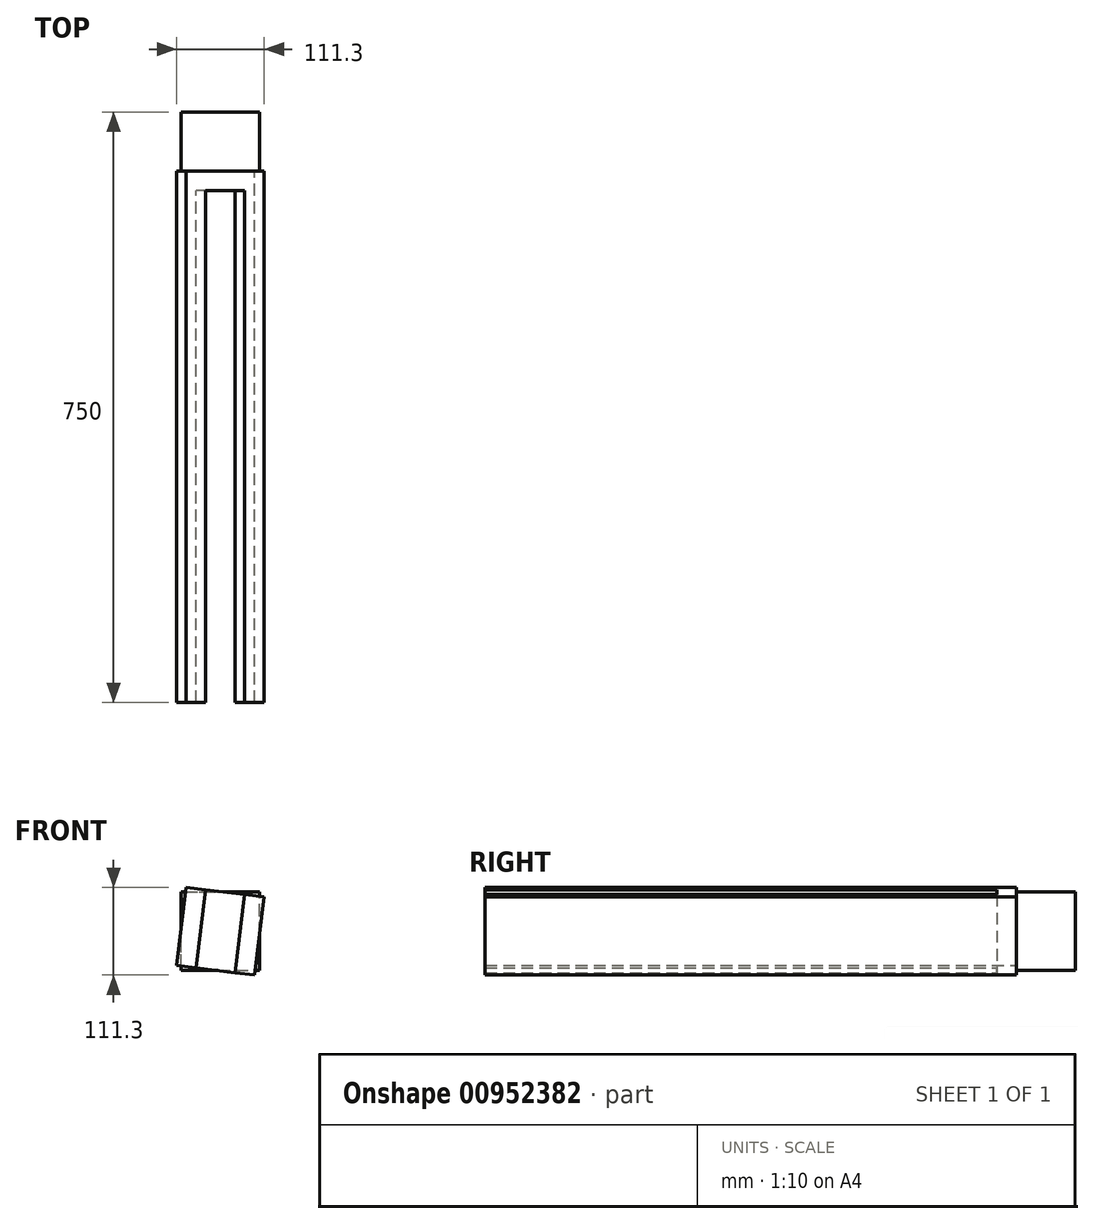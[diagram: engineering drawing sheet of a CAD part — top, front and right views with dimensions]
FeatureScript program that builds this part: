
annotation { "Feature Type Name" : "Feature", "Feature Type Description" : "" }
export const myFeature = defineFeature(function(context is Context, id is Id, definition is map)
    precondition{}
    {
        {
            var Q0;
            Q0=qCreatedBy(makeId("Front.planeOp"),FACE);
            var sketch = newSketch(context, id + "F0", { "sketchPlane" : qUnion([Q0])});
            skLineSegment(sketch, "E0.bottom", {"start": v(0, 0) * mm, "end": v(100, 0) * mm});
            skLineSegment(sketch, "E0.top", {"start": v(0, 100) * mm, "end": v(100, 100) * mm});
            skLineSegment(sketch, "E0.left", {"start": v(0, 0) * mm, "end": v(0, 100) * mm});
            skLineSegment(sketch, "E0.right", {"start": v(100, 0) * mm, "end": v(100, 100) * mm});
            skSolve(sketch);
        }
        {
            var Q0;
            Q0 = qSketchRegion(id + "F0", true);
            extrude(context, id + "F1", {"entities" : qUnion([Q0]), "depth" : 75 * mm, "offsetDistance" : 25 * mm});
        }
        {
            var Q0;
            Q0=makeQuery(id+"F1.opExtrude","CAP_FACE",FACE,{"disambiguationData":[OSD([sQuery(id+"F0.wireOp",EDGE,"E0.bottom"),sQuery(id+"F0.wireOp",EDGE,"E0.top"),sQuery(id+"F0.wireOp",EDGE,"E0.left"),sQuery(id+"F0.wireOp",EDGE,"E0.right")])],"isStart":false});
            var sketch = newSketch(context, id + "F2", { "sketchPlane" : qUnion([Q0])});
            skLineSegment(sketch, "E1", {"start": v(-5.65, 6.38) * mm, "end": v(6.38, 105.65) * mm});
            skLineSegment(sketch, "E2", {"start": v(6.38, 105.65) * mm, "end": v(105.65, 93.62) * mm});
            skLineSegment(sketch, "E3", {"start": v(105.65, 93.62) * mm, "end": v(93.62, -5.65) * mm});
            skLineSegment(sketch, "E4", {"start": v(93.62, -5.65) * mm, "end": v(-5.65, 6.38) * mm});
            skLineSegment(sketch, "E5", {"start": v(0, 100) * mm, "end": v(100, 0) * mm});
            skLineSegment(sketch, "E6", {"start": v(100, 0) * mm, "end": v(100, 100) * mm});
            skLineSegment(sketch, "E7", {"start": v(100, 100) * mm, "end": v(0, 0) * mm});
            skSolve(sketch);
        }
        {
            var Q0;
            {var subQ0=sQuery(id+"F2.wireOp",EDGE,"E3");var subQ1=sQuery(id+"F2.wireOp",EDGE,"E2");var subQ2=makeQuery(id+"F2.imprint","INTERSECT",VERTEX,{"derivedFrom":[subQ1,subQ0]});Q0=makeQuery(id+"F2.imprint","IMPRINT",FACE,{"disambiguationData":[TD([[makeQuery(id+"F2.imprint","IMPRINT",EDGE,{"disambiguationData":[TD([[subQ2,1.0]])],"derivedFrom":subQ1}),-1.0]])]});}
            var Q1;
            {var subQ5=sQuery(id+"F2.wireOp",EDGE,"E6");var subQ7=sQuery(id+"F2.wireOp",EDGE,"E2");var subQ8=makeQuery(id+"F2.imprint","INTERSECT",VERTEX,{"derivedFrom":[subQ7,subQ5]});Q1=makeQuery(id+"F2.imprint","IMPRINT",FACE,{"disambiguationData":[TD([[makeQuery(id+"F2.imprint","IMPRINT",EDGE,{"disambiguationData":[TD([[subQ8,1.0]])],"derivedFrom":subQ7}),-1.0]])]});}
            var Q2;
            {var subQ0=sQuery(id+"F2.wireOp",EDGE,"E4");var subQ1=sQuery(id+"F2.wireOp",EDGE,"E1");var subQ2=makeQuery(id+"F2.imprint","INTERSECT",VERTEX,{"derivedFrom":[subQ1,subQ0]});Q2=makeQuery(id+"F2.imprint","IMPRINT",FACE,{"disambiguationData":[TD([[makeQuery(id+"F2.imprint","IMPRINT",EDGE,{"disambiguationData":[TD([[subQ2,-1.0]])],"derivedFrom":subQ1}),-1.0]])]});}
            var Q3;
            {var subQ0=sQuery(id+"F2.wireOp",EDGE,"E2");var subQ1=sQuery(id+"F2.wireOp",EDGE,"E1");var subQ2=makeQuery(id+"F2.imprint","INTERSECT",VERTEX,{"derivedFrom":[subQ1,subQ0]});Q3=makeQuery(id+"F2.imprint","IMPRINT",FACE,{"disambiguationData":[TD([[makeQuery(id+"F2.imprint","IMPRINT",EDGE,{"disambiguationData":[TD([[subQ2,1.0]])],"derivedFrom":subQ1}),-1.0]])]});}
            var Q4;
            {var subQ0=sQuery(id+"F2.wireOp",EDGE,"E4");var subQ1=sQuery(id+"F2.wireOp",EDGE,"E3");var subQ2=makeQuery(id+"F2.imprint","INTERSECT",VERTEX,{"derivedFrom":[subQ1,subQ0]});Q4=makeQuery(id+"F2.imprint","IMPRINT",FACE,{"disambiguationData":[TD([[makeQuery(id+"F2.imprint","IMPRINT",EDGE,{"disambiguationData":[TD([[subQ2,1.0]])],"derivedFrom":subQ1}),-1.0]])]});}
            var Q5;
            {var subQ3=sQuery(id+"F2.wireOp",EDGE,"E5");var subQ5=sQuery(id+"F2.wireOp",EDGE,"E1");var subQ6=makeQuery(id+"F2.imprint","INTERSECT",VERTEX,{"derivedFrom":[subQ5,subQ3]});Q5=makeQuery(id+"F2.imprint","IMPRINT",FACE,{"disambiguationData":[TD([[makeQuery(id+"F2.imprint","IMPRINT",EDGE,{"disambiguationData":[TD([[subQ6,-1.0]])],"derivedFrom":subQ5}),-1.0]])]});}
            var Q6;
            {var subQ0=sQuery(id+"F2.wireOp",EDGE,"E5");var subQ1=sQuery(id+"F2.wireOp",EDGE,"E3");var subQ2=makeQuery(id+"F2.imprint","INTERSECT",VERTEX,{"derivedFrom":[subQ1,subQ0]});Q6=makeQuery(id+"F2.imprint","IMPRINT",FACE,{"disambiguationData":[TD([[makeQuery(id+"F2.imprint","IMPRINT",EDGE,{"disambiguationData":[TD([[subQ2,-1.0]])],"derivedFrom":subQ1}),-1.0]])]});}
            var Q7;
            {var subQ4=sQuery(id+"F2.wireOp",EDGE,"HYPdAmQG-CzOh-xeIb-K1Wl-egndXK9ylAPy");Q7=makeQuery(id+"F2.imprint","IMPRINT",FACE,{"disambiguationData":[TD([[makeQuery(id+"F2.imprint","IMPRINT",EDGE,{"derivedFrom":subQ4}),-1.0]])]});}
            var Q8;
            {var subQ0=sQuery(id+"F2.wireOp",EDGE,"3lIvViu7-IiRF-yCJw-prBx-l3yzu4JQAyZ1");Q8=makeQuery(id+"F2.imprint","IMPRINT",FACE,{"disambiguationData":[TD([[makeQuery(id+"F2.imprint","IMPRINT",EDGE,{"derivedFrom":subQ0}),-1.0]])]});}
            var Q9;
            {var subQ3=sQuery(id+"F2.wireOp",EDGE,"E5");var subQ7=sQuery(id+"F2.wireOp",EDGE,"E1");var subQ8=makeQuery(id+"F2.imprint","INTERSECT",VERTEX,{"derivedFrom":[subQ7,subQ3]});Q9=makeQuery(id+"F2.imprint","IMPRINT",FACE,{"disambiguationData":[TD([[makeQuery(id+"F2.imprint","IMPRINT",EDGE,{"disambiguationData":[TD([[subQ8,1.0]])],"derivedFrom":subQ7}),-1.0]])]});}
            extrude(context, id + "F3", {"entities" : qUnion([Q0, Q1, Q2, Q3, Q4, Q5, Q6, Q7, Q8, Q9]), "operationType" : NewBodyOperationType.ADD, "depth" : 25 * mm, "offsetDistance" : 25 * mm});
        }
        {
            var Q0;
            Q0=makeQuery(id+"F3.opExtrude","CAP_FACE",FACE,{"disambiguationData":[OSD([sQuery(id+"F2.wireOp",EDGE,"E1"),sQuery(id+"F2.wireOp",EDGE,"E2"),sQuery(id+"F2.wireOp",EDGE,"E3"),sQuery(id+"F2.wireOp",EDGE,"E4")])],"isStart":false});
            var sketch = newSketch(context, id + "F4", { "sketchPlane" : qUnion([Q0])});
            skLineSegment(sketch, "E8", {"start": v(6.38, 105.65) * mm, "end": v(31.2, 102.65) * mm});
            skLineSegment(sketch, "E9", {"start": v(31.2, 102.65) * mm, "end": v(19.17, 3.37) * mm});
            skLineSegment(sketch, "E10", {"start": v(19.17, 3.37) * mm, "end": v(-5.65, 6.38) * mm});
            skLineSegment(sketch, "E11", {"start": v(-5.65, 6.38) * mm, "end": v(6.38, 105.65) * mm});
            skLineSegment(sketch, "E12", {"start": v(105.65, 93.62) * mm, "end": v(80.84, 96.63) * mm});
            skLineSegment(sketch, "E13", {"start": v(80.84, 96.63) * mm, "end": v(68.8, -2.64) * mm});
            skLineSegment(sketch, "E14", {"start": v(68.8, -2.64) * mm, "end": v(93.62, -5.65) * mm});
            skLineSegment(sketch, "E15", {"start": v(93.62, -5.65) * mm, "end": v(105.65, 93.62) * mm});
            skSolve(sketch);
        }
        {
            var Q0;
            Q0 = qSketchRegion(id + "F4", true);
            extrude(context, id + "F5", {"entities" : qUnion([Q0]), "operationType" : NewBodyOperationType.ADD, "depth" : 650 * mm, "offsetDistance" : 25 * mm});
        }
    });
